# Revit family: Albardilla MJ. C-1
name_source: partatom
category: Modelos genéricos
units: mm (PartAtom-declared; Revit-internal decimal feet)

## family parameters
Compartido = No
Corte con vacíos al cargar = No
Cota de conector redondo = Diámetro de uso
Puede alojar armadura = No
Punto de cálculo de habitación = No
Se basa en plano de trabajo = No
Siempre vertical = No
Tipo de pieza = Normal

## types (10) — shared parameters
Descripción = Pieza de hormigón polímero con anclaje de acero inoxidable.
Fabricante = ULMA Architectural Solutions
Material = Hormigón polímero STONEO. Color C-1
URL = https://www.ulmaarchitectural.com
zero-valued in all types: Elevación por defecto

## per-type parameters (varying)
| type | Ancho | Ancho doble | Ancho total | Modelo | Visible dos líneas | Visible una linea |
| MJ12 | 125 mm  [stored 0.410105 ft] | 31 mm | 175 mm  [stored 0.574147 ft] | Albardilla MJ12 | No | Sí |
| MJ14 | 150 mm | 38 mm | 200 mm  [stored 0.656168 ft] | Albardilla MJ14 | No | Sí |
| MJ17 | 170 mm  [stored 0.557743 ft] | 43 mm | 220 mm  [stored 0.721785 ft] | Albardilla MJ17 | No | Sí |
| MJ19 | 205 mm  [stored 0.672572 ft] | 51 mm | 255 mm  [stored 0.836614 ft] | Albardilla MJ19 | No | Sí |
| MJ22 | 220 mm  [stored 0.721785 ft] | 55 mm  [stored 0.180446 ft] | 270 mm  [stored 0.885827 ft] | Albardilla MJ22 | No | Sí |
| MJ25 | 255 mm  [stored 0.836614 ft] | 64 mm | 305 mm  [stored 1.00066 ft] | Albardilla MJ25 | No | Sí |
| MJ30 | 305 mm  [stored 1.00066 ft] | 76 mm | 355 mm | Albardilla MJ30 | Sí | No |
| MJ35 | 350 mm  [stored 1.14829 ft] | 88 mm | 400 mm  [stored 1.31234 ft] | Albardilla MJ35 | Sí | No |
| MJ40 | 400 mm  [stored 1.31234 ft] | 100 mm  [stored 0.328084 ft] | 450 mm  [stored 1.47638 ft] | Albardilla MJ40 | Sí | No |
| MJ27 | 270 mm  [stored 0.885827 ft] | 68 mm | 320 mm  [stored 1.04987 ft] | Albardilla MJ27 | No | Sí |

note: column(s) folded — value = type name in every type: Código de montaje

note: [stored X ft] marks values corroborated as IEEE doubles in the binary element streams (Revit-internal decimal feet)
